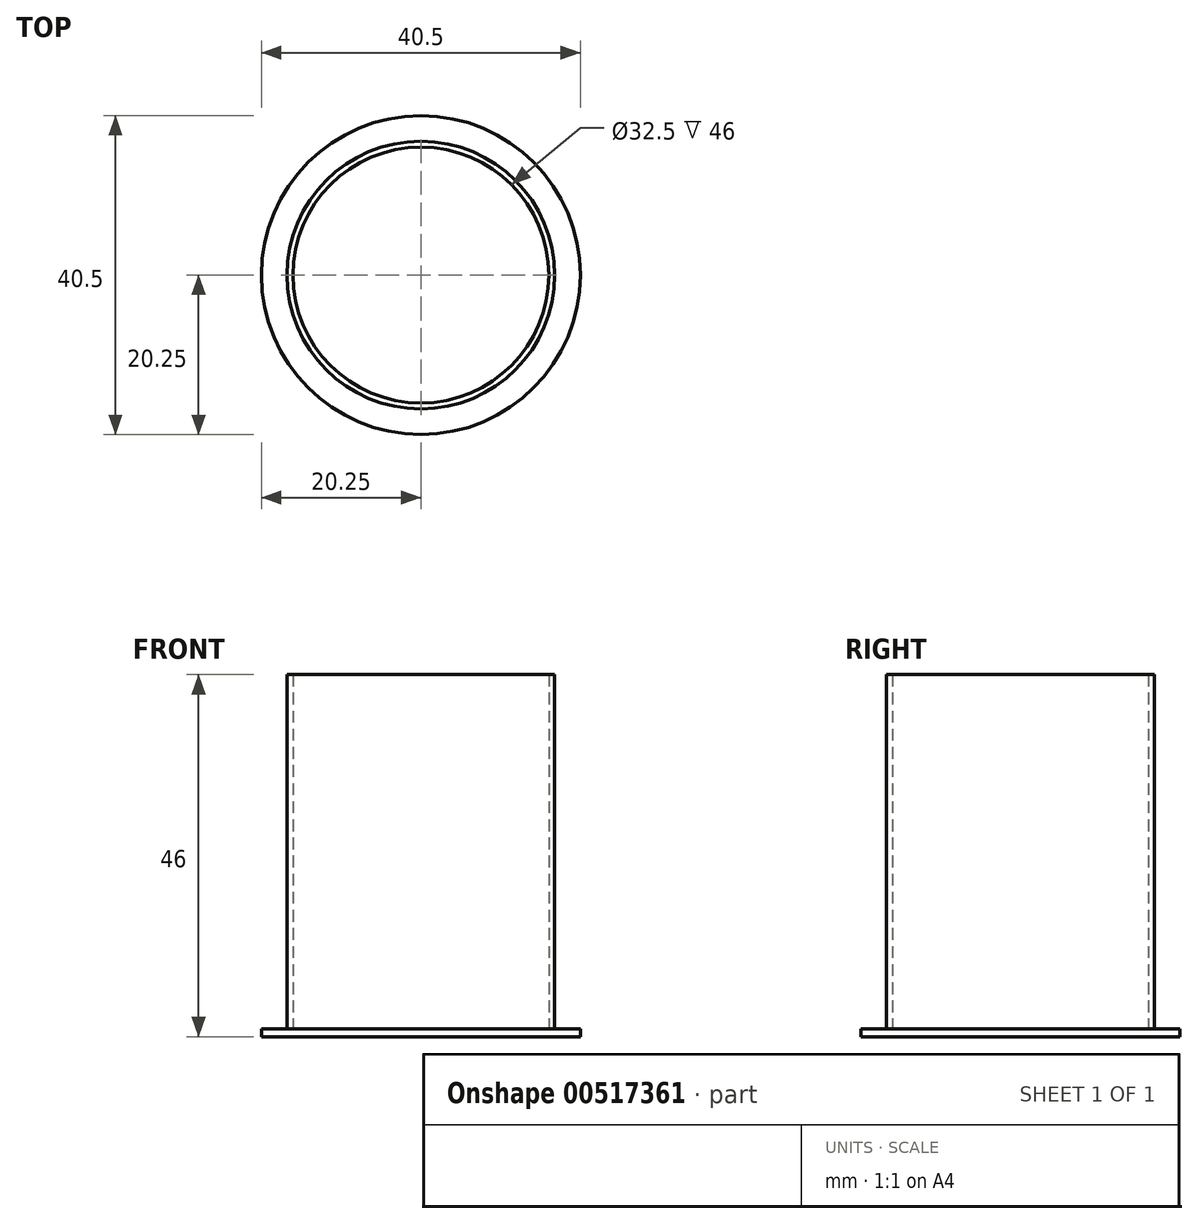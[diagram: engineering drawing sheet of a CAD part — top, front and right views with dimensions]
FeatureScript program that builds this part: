
annotation { "Feature Type Name" : "Feature", "Feature Type Description" : "" }
export const myFeature = defineFeature(function(context is Context, id is Id, definition is map)
    precondition{}
    {
        {
            var Q0;
            Q0=qCreatedBy(makeId("Top.planeOp"),FACE);
            var sketch = newSketch(context, id + "F0", { "sketchPlane" : qUnion([Q0])});
            skCircle(sketch, "E0", {"center": v(0, 0) * mm, "radius": 16.25 * mm});
            skCircle(sketch, "E1.0", {"center": v(0, 0) * mm, "radius": 20.25 * mm});
            skSolve(sketch);
        }
        {
            var Q0;
            Q0 = qSketchRegion(id + "F0", true);
            extrude(context, id + "F1", {"entities" : qUnion([Q0]), "depth" : 1 * mm, "offsetDistance" : 25 * mm});
        }
        {
            var Q0;
            Q0=makeQuery(id+"F1.opExtrude","CAP_FACE",FACE,{"disambiguationData":[OSD([sQuery(id+"F0.wireOp",EDGE,"E0"),sQuery(id+"F0.wireOp",EDGE,"E1.0")])],"isStart":false});
            var sketch = newSketch(context, id + "F2", { "sketchPlane" : qUnion([Q0])});
            skCircle(sketch, "E2", {"center": v(0, 0) * mm, "radius": 17 * mm});
            skSolve(sketch);
        }
        {
            var Q0;
            Q0=makeQuery(id+"F2.imprint","IMPRINT",FACE,{"disambiguationData":[TD([[makeQuery(id+"F2.imprint","IMPRINT",EDGE,{"derivedFrom":sQuery(id+"F2.wireOp",EDGE,"E2")}),1.0]])]});
            extrude(context, id + "F3", {"entities" : qUnion([Q0]), "operationType" : NewBodyOperationType.ADD, "depth" : 45 * mm, "offsetDistance" : 25 * mm});
        }
    });
